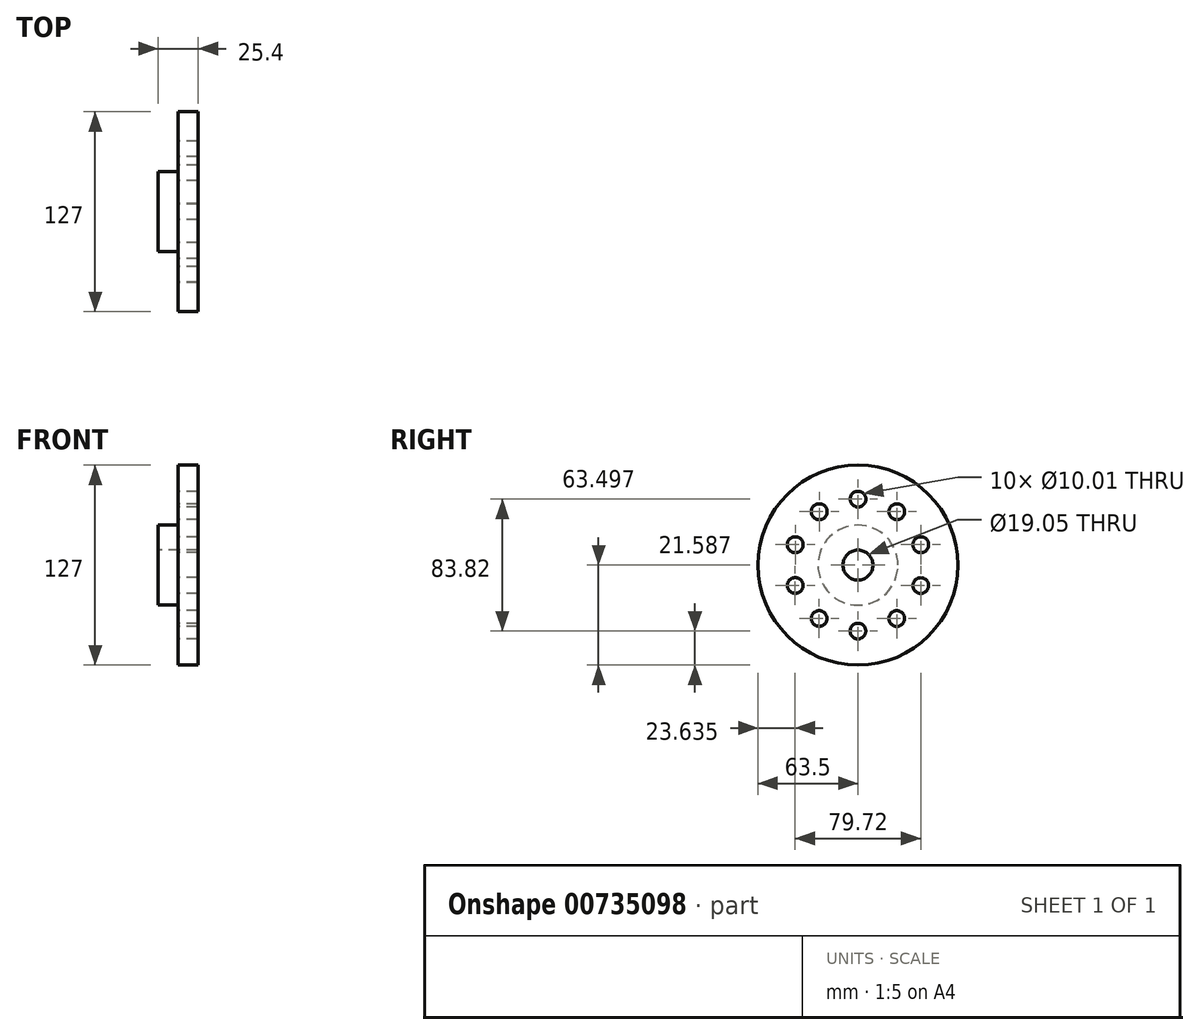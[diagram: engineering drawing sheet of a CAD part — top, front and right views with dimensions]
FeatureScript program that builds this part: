
annotation { "Feature Type Name" : "Feature", "Feature Type Description" : "" }
export const myFeature = defineFeature(function(context is Context, id is Id, definition is map)
    precondition{}
    {
        {
            var Q0;
            Q0=qCreatedBy(makeId("Front.planeOp"),FACE);
            var sketch = newSketch(context, id + "F0", { "sketchPlane" : qUnion([Q0])});
            skLineSegment(sketch, "E0", {"start": v(-25.15, 29.47) * mm, "end": v(-12.45, 29.47) * mm});
            skLineSegment(sketch, "E1", {"start": v(-12.45, 29.47) * mm, "end": v(-12.45, -24.5) * mm});
            skLineSegment(sketch, "E2", {"start": v(-12.45, -24.5) * mm, "end": v(-37.85, -24.5) * mm});
            skLineSegment(sketch, "E3", {"start": v(-37.85, -24.5) * mm, "end": v(-37.85, -8.63) * mm});
            skLineSegment(sketch, "E4", {"start": v(-37.85, -8.63) * mm, "end": v(-25.15, -8.63) * mm});
            skLineSegment(sketch, "E5", {"start": v(-25.15, -8.63) * mm, "end": v(-25.15, 29.47) * mm});
            skLineSegment(sketch, "E6", {"start": v(-74.45, -34.03) * mm, "end": v(16.18, -34.03) * mm, "construction": true});
            skSolve(sketch);
        }
        {
            var Q0;
            Q0=qSketchRegion(id+"F0",true);
            var Q1;
            Q1=sQuery(id+"F0.wireOp",EDGE,"E6");
            revolve(context, id + "F1", {"entities" : qUnion([Q0]), "axis" : qUnion([Q1]), "revolveType" : RevolveType.FULL});
        }
        {
            var Q0;
            Q0=makeQuery(id+"F1.opRevolve","SWEPT_FACE",FACE,{"disambiguationData":[OSD([sQuery(id+"F0.wireOp",EDGE,"E5")])]});
            var sketch = newSketch(context, id + "F2", { "sketchPlane" : qUnion([Q0])});
            skCircle(sketch, "E7", {"center": v(0, -34.03) * mm, "radius": 41.91 * mm, "construction": true});
            skCircle(sketch, "E8", {"center": v(0, 7.88) * mm, "radius": 5 * mm});
            skCircle(sketch, "E9", {"center": v(24.63, -0.12) * mm, "radius": 5 * mm});
            skCircle(sketch, "E10", {"center": v(39.85, -21.07) * mm, "radius": 5 * mm});
            skCircle(sketch, "E11", {"center": v(39.87, -46.96) * mm, "radius": 5 * mm});
            skCircle(sketch, "E12", {"center": v(24.66, -67.92) * mm, "radius": 5 * mm});
            skCircle(sketch, "E13", {"center": v(-24.6, -67.96) * mm, "radius": 5 * mm});
            skCircle(sketch, "E14", {"center": v(0.03, -75.94) * mm, "radius": 5 * mm});
            skCircle(sketch, "E15", {"center": v(-39.84, -47.03) * mm, "radius": 5 * mm});
            skCircle(sketch, "E16", {"center": v(-39.85, -21.07) * mm, "radius": 5 * mm});
            skCircle(sketch, "E17", {"center": v(-24.63, -0.12) * mm, "radius": 5 * mm});
            skLineSegment(sketch, "E18", {"start": v(0, -34.03) * mm, "end": v(41.91, -34.03) * mm});
            skSolve(sketch);
        }
        {
            var Q0;
            Q0=qSketchRegion(id+"F2",true);
            extrude(context, id + "F3", {"entities" : qUnion([Q0]), "operationType" : NewBodyOperationType.REMOVE, "oppositeDirection" : true, "depth" : 25.4 * mm, "offsetDistance" : 25.4 * mm});
        }
    });
